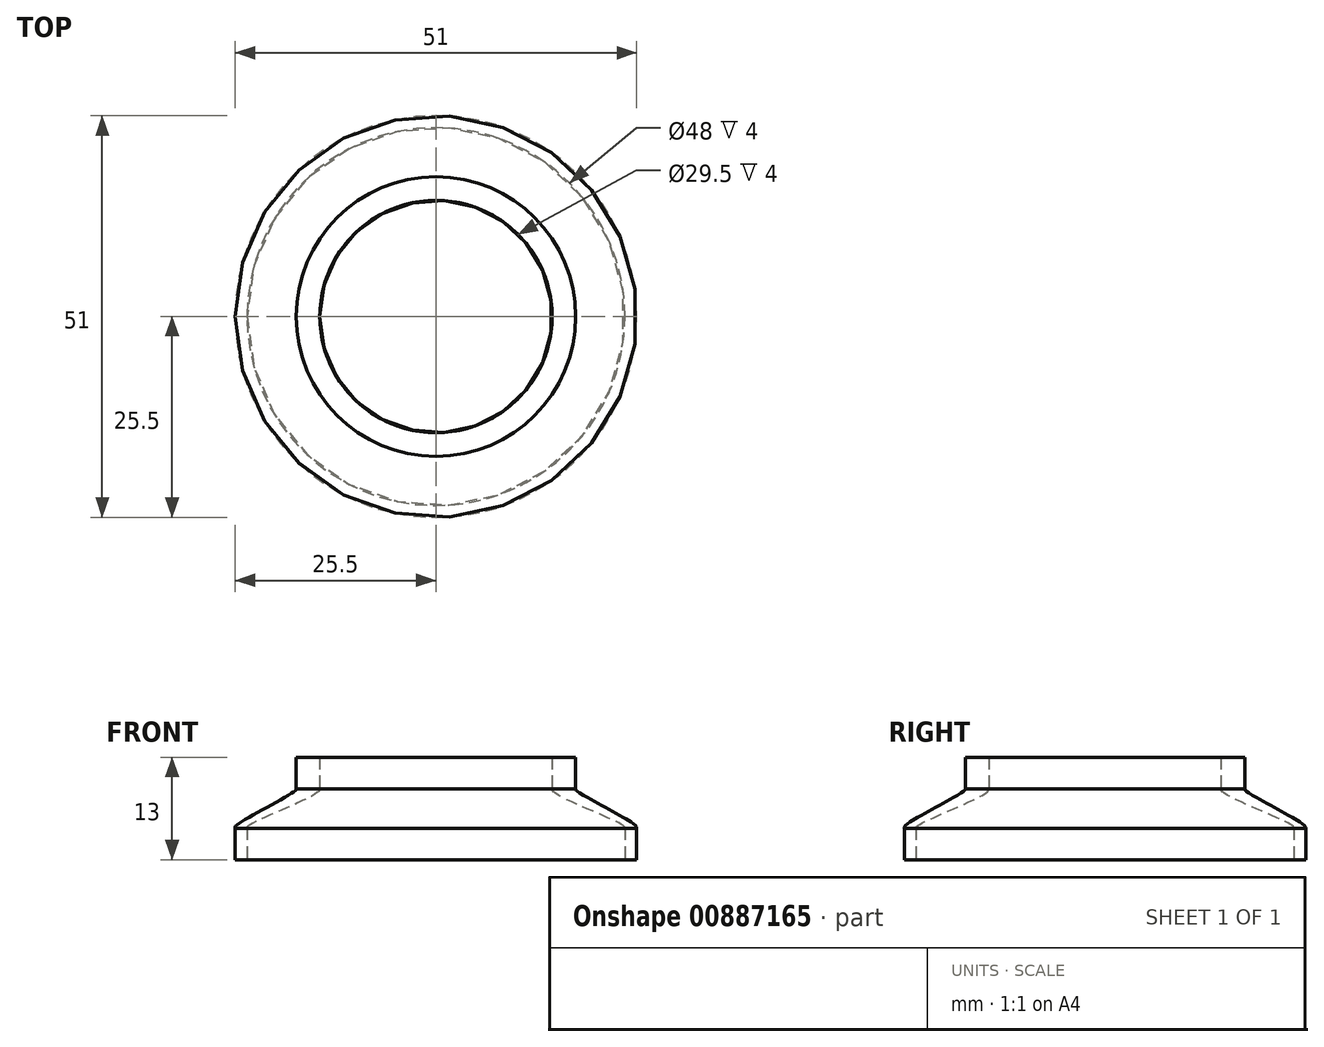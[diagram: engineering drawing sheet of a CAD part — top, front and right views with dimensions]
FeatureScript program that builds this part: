
annotation { "Feature Type Name" : "Feature", "Feature Type Description" : "" }
export const myFeature = defineFeature(function(context is Context, id is Id, definition is map)
    precondition{}
    {
        {
            var Q0;
            Q0=qCreatedBy(makeId("Front.planeOp"),FACE);
            var sketch = newSketch(context, id + "F0", { "sketchPlane" : qUnion([Q0])});
            skLineSegment(sketch, "E0", {"start": v(0, 0) * mm, "end": v(0, 13) * mm});
            skLineSegment(sketch, "E1", {"start": v(-25.5, 0) * mm, "end": v(-25.5, 4) * mm});
            skLineSegment(sketch, "E2", {"start": v(-17.75, 13) * mm, "end": v(-17.75, 9) * mm});
            skFitSpline(sketch, "E3", {"points": [v(-17.75, 9) * mm, v(-17.86, 8.78) * mm, v(-25.37, 4.33) * mm, v(-25.5, 4) * mm], "startDerivative": vector(-0.02, -0.67) * mm, "endDerivative": vector(-0.06, -1.28) * mm});
            skLineSegment(sketch, "E4", {"start": v(-25.5, 0) * mm, "end": v(-24, 0) * mm});
            skLineSegment(sketch, "E5", {"start": v(-17.75, 13) * mm, "end": v(-14.75, 13) * mm});
            skLineSegment(sketch, "E6", {"start": v(-14.75, 13) * mm, "end": v(-14.75, 9) * mm});
            skLineSegment(sketch, "E7", {"start": v(-24, 0) * mm, "end": v(-24, 4) * mm});
            skFitSpline(sketch, "E8", {"points": [v(-14.75, 9) * mm, v(-14.94, 8.64) * mm, v(-23.88, 4.28) * mm, v(-24, 4) * mm], "startDerivative": vector(0, -0.43) * mm, "endDerivative": vector(0, -1.81) * mm});
            skSolve(sketch);
        }
        {
            var Q0;
            Q0=makeQuery(id+"F0.imprint","IMPRINT",FACE,{"disambiguationData":[TD([[makeQuery(id+"F0.imprint","IMPRINT",EDGE,{"derivedFrom":sQuery(id+"F0.wireOp",EDGE,"E1")}),-1.0]])]});
            var Q1;
            Q1=sQuery(id+"F0.wireOp",EDGE,"E0");
            revolve(context, id + "F1", {"surfaceOperationType" : NewSurfaceOperationType.NEW, "entities" : qUnion([Q0]), "axis" : qUnion([Q1]), "revolveType" : RevolveType.FULL});
        }
    });
